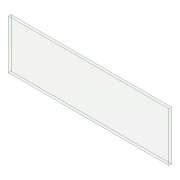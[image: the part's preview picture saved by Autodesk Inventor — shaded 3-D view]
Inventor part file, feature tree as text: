
AUTODESK INVENTOR PART (.ipt)
format: ipt  version: 2018.3 (Build 223284000, 284)  size: 73,728 bytes
history: native  units: in
note: dims shown in document units (in); Inventor stores cm internally (conversion verified against a paired STEP export)
features: extrude x1, sketch x1
ambient origin geometry x8: Origin, YZ Plane, XZ Plane, XY Plane, X Axis, Y Axis, Z Axis, Center Point
bodies: Solid1 (feature_tree)
feature tree (2):
  extrude  "Extrusion1"  Depth=0.56in
  sketch  "Sketch1"  dims[d0=1.83in d1=0.56in d2=0.03in d3=0.0in]
